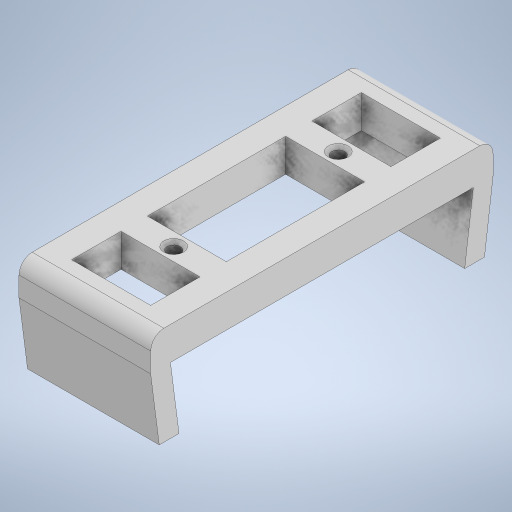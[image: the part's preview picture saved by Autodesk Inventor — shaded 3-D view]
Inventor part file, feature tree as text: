
AUTODESK INVENTOR PART (.ipt)
format: ipt  version: 2023 (Build 270158000, 158)  size: 279,040 bytes
history: native  units: mm
features: sketch x3, extrude x2, other x1, hole x1, fillet x1
ambient origin geometry x8: Origin, YZ Plane, XZ Plane, XY Plane, X Axis, Y Axis, Z Axis, Center Point
bodies: Body1 (feature_tree)
feature tree (8):
  other  "솔리드1"
  extrude  "돌출1"  Depth=20.0mm
  hole  "구멍1"  [1 undecoded]
  extrude  "돌출2"  Depth=4.0mm
  fillet  "모깎기1"  Radius=15.5mm
  sketch  "스케치1"
  sketch  "스케치2"
  sketch  "스케치3"
note: 1 required parameter value undecoded (feature->parameter linkage not recoverable at this tier; creation-order binding heuristic only, values carry confidence <= 0.55)
